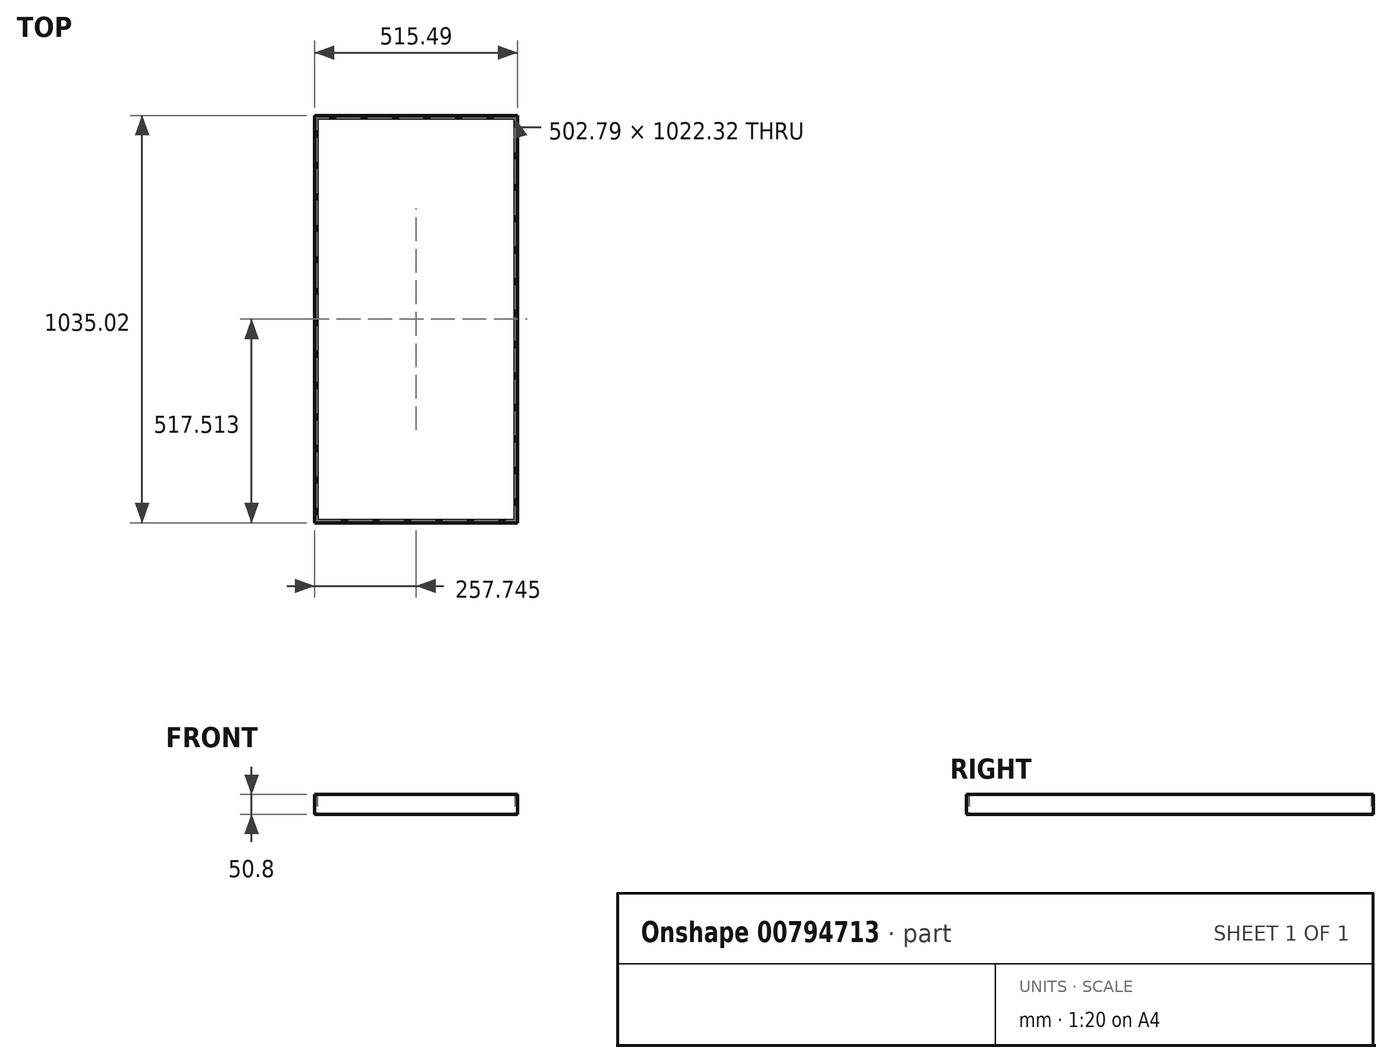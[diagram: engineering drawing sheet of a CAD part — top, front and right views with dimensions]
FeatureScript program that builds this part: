
annotation { "Feature Type Name" : "Feature", "Feature Type Description" : "" }
export const myFeature = defineFeature(function(context is Context, id is Id, definition is map)
    precondition{}
    {
        {
            var Q0;
            Q0=qCreatedBy(makeId("Top.planeOp"),FACE);
            var sketch = newSketch(context, id + "F0", { "sketchPlane" : qUnion([Q0])});
            skLineSegment(sketch, "E0.bottom", {"start": v(-33.27, -26.99) * mm, "end": v(482.22, -26.99) * mm});
            skLineSegment(sketch, "E0.top", {"start": v(-33.27, 1008.03) * mm, "end": v(482.22, 1008.03) * mm});
            skLineSegment(sketch, "E0.left", {"start": v(-33.27, -26.99) * mm, "end": v(-33.27, 1008.03) * mm});
            skLineSegment(sketch, "E0.right", {"start": v(482.22, -26.99) * mm, "end": v(482.22, 1008.03) * mm});
            skLineSegment(sketch, "E1.0", {"start": v(-26.92, -20.64) * mm, "end": v(-26.92, 1001.68) * mm});
            skLineSegment(sketch, "E1.1", {"start": v(-26.92, -20.64) * mm, "end": v(475.87, -20.64) * mm});
            skLineSegment(sketch, "E1.2", {"start": v(475.87, -20.64) * mm, "end": v(475.87, 1001.68) * mm});
            skLineSegment(sketch, "E1.3", {"start": v(-26.92, 1001.68) * mm, "end": v(475.87, 1001.68) * mm});
            skSolve(sketch);
        }
        {
            var Q0;
            Q0 = qSketchRegion(id + "F0", true);
            extrude(context, id + "F1", {"entities" : qUnion([Q0]), "depth" : 25.4 * mm, "offsetDistance" : 25.4 * mm});
        }
        {
            var Q0;
            Q0=makeQuery(id+"F1.opExtrude","CAP_FACE",FACE,{"disambiguationData":[OSD([sQuery(id+"F0.wireOp",EDGE,"E0.bottom"),sQuery(id+"F0.wireOp",EDGE,"E0.top"),sQuery(id+"F0.wireOp",EDGE,"E0.left"),sQuery(id+"F0.wireOp",EDGE,"E0.right"),sQuery(id+"F0.wireOp",EDGE,"E1.0"),sQuery(id+"F0.wireOp",EDGE,"E1.1"),sQuery(id+"F0.wireOp",EDGE,"E1.2"),sQuery(id+"F0.wireOp",EDGE,"E1.3")])],"isStart":false});
            extrude(context, id + "F2", {"entities" : qUnion([Q0]), "operationType" : NewBodyOperationType.ADD, "depth" : 25.4 * mm, "offsetDistance" : 25.4 * mm});
        }
    });
